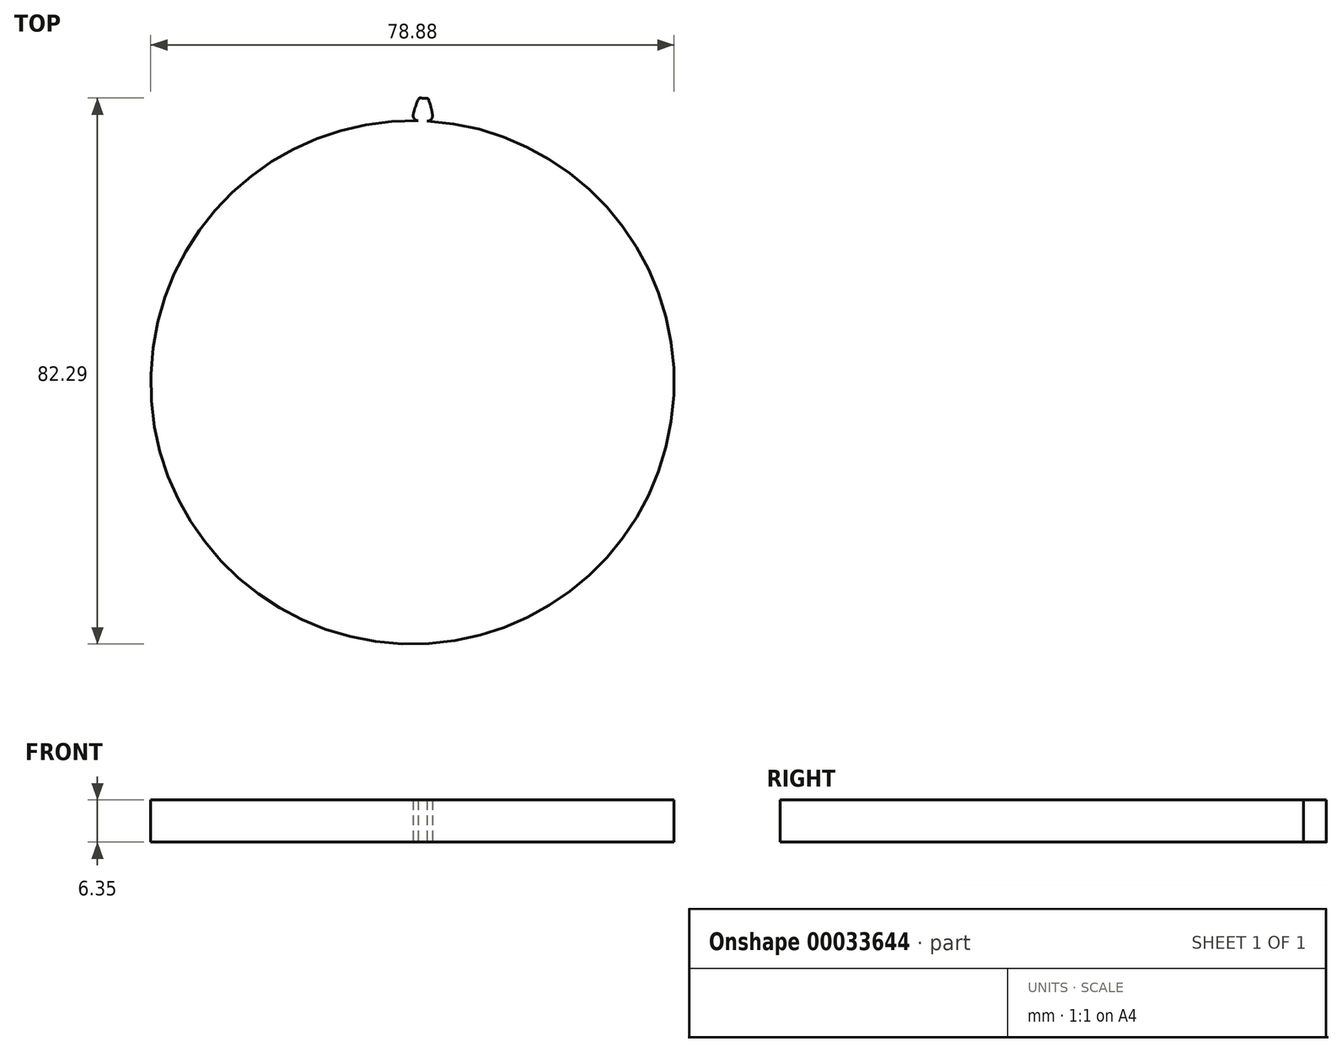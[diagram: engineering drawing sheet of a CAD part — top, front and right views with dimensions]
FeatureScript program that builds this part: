
annotation { "Feature Type Name" : "Feature", "Feature Type Description" : "" }
export const myFeature = defineFeature(function(context is Context, id is Id, definition is map)
    precondition{}
    {
        {
            assignVariable(context, id + "F0", {"name" : "N", "anyValue" : 16 * 3.25});
        }
        {
            var Q0;
            Q0=qCreatedBy(makeId("Top.planeOp"),FACE);
            var sketch = newSketch(context, id + "F1", { "sketchPlane" : qUnion([Q0])});
            skCircle(sketch, "E0", {"center": v(0, 0) * mm, "radius": 39.47 * mm, "construction": true});
            skCircle(sketch, "E1", {"center": v(0, 0) * mm, "radius": 41.28 * mm, "construction": true});
            skCircle(sketch, "E2", {"center": v(0, 0) * mm, "radius": 42.86 * mm});
            skLineSegment(sketch, "E3", {"start": v(0, 0) * mm, "end": v(0, 39.47) * mm, "construction": true});
            skLineSegment(sketch, "E4", {"start": v(0, 0) * mm, "end": v(2.58, 39.39) * mm, "construction": true});
            skLineSegment(sketch, "E5", {"start": v(0, 0) * mm, "end": v(5.15, 39.13) * mm, "construction": true});
            skLineSegment(sketch, "E6", {"start": v(0, 0) * mm, "end": v(7.7, 38.71) * mm, "construction": true});
            skLineSegment(sketch, "E7", {"start": v(0, 0) * mm, "end": v(10.22, 38.13) * mm, "construction": true});
            skCircle(sketch, "E8", {"center": v(0, 0) * mm, "radius": 39.44 * mm});
            skLineSegment(sketch, "E9", {"start": v(2.58, 39.39) * mm, "end": v(0, 39.56) * mm, "construction": true});
            skLineSegment(sketch, "E10", {"start": v(5.15, 39.13) * mm, "end": v(0.03, 39.8) * mm, "construction": true});
            skLineSegment(sketch, "E11", {"start": v(7.7, 38.71) * mm, "end": v(0.1, 40.23) * mm, "construction": true});
            skLineSegment(sketch, "E12", {"start": v(10.22, 38.13) * mm, "end": v(0.23, 40.8) * mm, "construction": true});
            skLineSegment(sketch, "E13", {"start": v(0, 0) * mm, "end": v(12.69, 37.38) * mm, "construction": true});
            skLineSegment(sketch, "E14", {"start": v(12.69, 37.38) * mm, "end": v(0.46, 41.53) * mm, "construction": true});
            skLineSegment(sketch, "E15", {"start": v(0, 0) * mm, "end": v(15.1, 36.47) * mm, "construction": true});
            skLineSegment(sketch, "E16", {"start": v(0, 0) * mm, "end": v(17.46, 35.4) * mm, "construction": true});
            skLineSegment(sketch, "E17", {"start": v(0, 0) * mm, "end": v(19.74, 34.18) * mm, "construction": true});
            skLineSegment(sketch, "E18", {"start": v(15.1, 36.47) * mm, "end": v(0.78, 42.4) * mm, "construction": true});
            skLineSegment(sketch, "E19", {"start": v(17.46, 35.4) * mm, "end": v(1.24, 43.4) * mm, "construction": true});
            skLineSegment(sketch, "E20", {"start": v(19.74, 34.18) * mm, "end": v(1.84, 44.52) * mm, "construction": true});
            skLineSegment(sketch, "E21", {"start": v(0, 0) * mm, "end": v(21.93, 32.82) * mm, "construction": true});
            skLineSegment(sketch, "E22", {"start": v(0, 0) * mm, "end": v(24.03, 31.31) * mm, "construction": true});
            skLineSegment(sketch, "E23", {"start": v(0, 0) * mm, "end": v(26.03, 29.68) * mm, "construction": true});
            skLineSegment(sketch, "E24", {"start": v(0, 0) * mm, "end": v(27.91, 27.91) * mm, "construction": true});
            skLineSegment(sketch, "E25", {"start": v(0, 0) * mm, "end": v(29.68, 26.03) * mm, "construction": true});
            skLineSegment(sketch, "E26", {"start": v(21.93, 32.82) * mm, "end": v(2.6, 45.74) * mm, "construction": true});
            skLineSegment(sketch, "E27", {"start": v(24.03, 31.31) * mm, "end": v(3.53, 47.04) * mm, "construction": true});
            skLineSegment(sketch, "E28", {"start": v(26.03, 29.68) * mm, "end": v(4.66, 48.41) * mm, "construction": true});
            skLineSegment(sketch, "E29", {"start": v(27.91, 27.91) * mm, "end": v(5.99, 49.83) * mm, "construction": true});
            skLineSegment(sketch, "E30", {"start": v(29.68, 26.03) * mm, "end": v(7.53, 51.28) * mm, "construction": true});
            skLineSegment(sketch, "E31", {"start": v(0, 0) * mm, "end": v(31.31, 24.03) * mm, "construction": true});
            skLineSegment(sketch, "E32", {"start": v(31.31, 24.03) * mm, "end": v(9.3, 52.72) * mm, "construction": true});
            skLineSegment(sketch, "E33", {"start": v(0, 0) * mm, "end": v(32.82, 21.93) * mm, "construction": true});
            skLineSegment(sketch, "E34", {"start": v(32.82, 21.93) * mm, "end": v(11.3, 54.15) * mm, "construction": true});
            skSolve(sketch);
        }
        {
            var Q0;
            Q0=qCreatedBy(makeId("Top.planeOp"),FACE);
            var sketch = newSketch(context, id + "F2", { "sketchPlane" : qUnion([Q0])});
            skLineSegment(sketch, "E35.0", {"start": v(31.31, 24.03) * mm, "end": v(9.3, 52.72) * mm, "construction": true});
            skLineSegment(sketch, "E35.1", {"start": v(29.68, 26.03) * mm, "end": v(7.53, 51.28) * mm, "construction": true});
            skLineSegment(sketch, "E35.2", {"start": v(27.91, 27.91) * mm, "end": v(5.99, 49.83) * mm, "construction": true});
            skLineSegment(sketch, "E35.3", {"start": v(26.03, 29.68) * mm, "end": v(4.66, 48.41) * mm, "construction": true});
            skLineSegment(sketch, "E35.4", {"start": v(24.03, 31.31) * mm, "end": v(3.53, 47.04) * mm, "construction": true});
            skLineSegment(sketch, "E35.5", {"start": v(21.93, 32.82) * mm, "end": v(2.6, 45.74) * mm, "construction": true});
            skLineSegment(sketch, "E35.6", {"start": v(19.74, 34.18) * mm, "end": v(1.84, 44.52) * mm, "construction": true});
            skLineSegment(sketch, "E35.7", {"start": v(17.46, 35.4) * mm, "end": v(1.24, 43.4) * mm, "construction": true});
            skLineSegment(sketch, "E35.8", {"start": v(15.1, 36.47) * mm, "end": v(0.78, 42.4) * mm, "construction": true});
            skLineSegment(sketch, "E35.9", {"start": v(12.69, 37.38) * mm, "end": v(0.46, 41.53) * mm, "construction": true});
            skLineSegment(sketch, "E35.10", {"start": v(10.22, 38.13) * mm, "end": v(0.23, 40.8) * mm, "construction": true});
            skLineSegment(sketch, "E35.11", {"start": v(7.7, 38.71) * mm, "end": v(0.1, 40.23) * mm, "construction": true});
            skLineSegment(sketch, "E35.12", {"start": v(5.15, 39.13) * mm, "end": v(0.03, 39.8) * mm, "construction": true});
            skLineSegment(sketch, "E35.13", {"start": v(2.58, 39.39) * mm, "end": v(0, 39.56) * mm, "construction": true});
            skCircle(sketch, "E35.14", {"center": v(0, 0) * mm, "radius": 39.47 * mm});
            skCircle(sketch, "E35.15", {"center": v(0, 0) * mm, "radius": 39.44 * mm});
            skCircle(sketch, "E35.16", {"center": v(0, 0) * mm, "radius": 41.28 * mm, "construction": true});
            skCircle(sketch, "E35.17", {"center": v(0, 0) * mm, "radius": 42.86 * mm});
            skLineSegment(sketch, "E36.0", {"start": v(32.82, 21.93) * mm, "end": v(11.3, 54.15) * mm, "construction": true});
            skLineSegment(sketch, "E37.0", {"start": v(0, 0) * mm, "end": v(0, 39.47) * mm, "construction": true});
            skFitSpline(sketch, "E38", {"points": [v(0, 39.47) * mm, v(0, 39.56) * mm, v(0.03, 39.8) * mm, v(0.1, 40.23) * mm, v(0.23, 40.8) * mm, v(0.46, 41.53) * mm, v(0.78, 42.4) * mm, v(1.24, 43.4) * mm, v(1.84, 44.52) * mm, v(2.6, 45.74) * mm, v(3.53, 47.04) * mm, v(4.66, 48.41) * mm, v(5.99, 49.83) * mm, v(7.53, 51.28) * mm, v(9.3, 52.72) * mm, v(11.3, 54.15) * mm, v(0, 0) * mm], "startDerivative": vector(0.89, 20.38) * mm, "endDerivative": vector(-106.5, -510.77) * mm});
            skLineSegment(sketch, "E39", {"start": v(0.37, 41.27) * mm, "end": v(0, 0) * mm, "construction": true});
            skLineSegment(sketch, "E40", {"start": v(0, 0) * mm, "end": v(1.68, 42.83) * mm, "construction": true});
            skFitSpline(sketch, "E41.MirrorCS", {"points": [v(3.1, 39.35) * mm, v(3.1, 39.43) * mm, v(3.1, 39.69) * mm, v(3.05, 40.1) * mm, v(2.96, 40.7) * mm, v(2.8, 41.44) * mm, v(2.54, 42.33) * mm, v(2.17, 43.36) * mm, v(1.66, 44.52) * mm, v(1, 45.8) * mm, v(0.16, 47.17) * mm, v(-0.85, 48.63) * mm, v(-2.07, 50.15) * mm, v(-3.5, 51.7) * mm, v(-5.14, 53.29) * mm, v(-7.01, 54.87) * mm, v(0, 0) * mm], "startDerivative": vector(0.71, 20.38) * mm, "endDerivative": vector(66.14, -517.54) * mm});
            skLineSegment(sketch, "E42", {"start": v(3.1, 39.35) * mm, "end": v(3.1, 39.32) * mm});
            skLineSegment(sketch, "E43", {"start": v(0, 39.47) * mm, "end": v(0, 39.44) * mm});
            skSolve(sketch);
        }
        {
            var Q0;
            {var subQ3=sQuery(id+"F2.wireOp",EDGE,"E41.MirrorCS");var subQ6=sQuery(id+"F2.wireOp",EDGE,"E35.17");var subQ8=makeQuery(id+"F2.imprint","INTERSECT",VERTEX,{"disambiguationData":[OD(1.0)],"derivedFrom":[subQ6,subQ3]});Q0=makeQuery(id+"F2.imprint","IMPRINT",FACE,{"disambiguationData":[TD([[makeQuery(id+"F2.imprint","IMPRINT",EDGE,{"disambiguationData":[TD([[subQ8,-1.0]])],"derivedFrom":subQ6}),1.0]])]});}
            var Q1;
            {var subQ3=sQuery(id+"F2.wireOp",EDGE,"E41.MirrorCS");var subQ5=sQuery(id+"F2.wireOp",EDGE,"E35.15");var subQ6=makeQuery(id+"F2.imprint","INTERSECT",VERTEX,{"derivedFrom":[subQ5,subQ3]});Q1=makeQuery(id+"F2.imprint","IMPRINT",FACE,{"disambiguationData":[TD([[makeQuery(id+"F2.imprint","IMPRINT",EDGE,{"disambiguationData":[TD([[subQ6,-1.0]])],"derivedFrom":subQ5}),1.0]])]});}
            var Q2;
            {var subQ2=sQuery(id+"F2.wireOp",EDGE,"E42");Q2=makeQuery(id+"F2.imprint","IMPRINT",FACE,{"disambiguationData":[TD([[makeQuery(id+"F2.imprint","IMPRINT",EDGE,{"derivedFrom":subQ2}),-1.0]])]});}
            extrude(context, id + "F3", {"entities" : qUnion([Q0, Q1, Q2]), "depth" : 6.35 * mm, "offsetDistance" : 25.4 * mm});
        }
        {
            var Q0;
            Q0=makeQuery(id+"F3.opExtrude","SWEPT_EDGE",EDGE,{"disambiguationData":[OSD([sQuery(id+"F2.wireOp",EDGE,"E35.17"),sQuery(id+"F2.wireOp",EDGE,"E38")])]});
            var Q1;
            Q1=makeQuery(id+"F3.opExtrude","SWEPT_EDGE",EDGE,{"disambiguationData":[OSD([sQuery(id+"F2.wireOp",EDGE,"E35.17"),sQuery(id+"F2.wireOp",EDGE,"E41.MirrorCS")])]});
            fillet(context, id + "F4", {"entities" : qUnion([Q0, Q1]), "radius" : 0.25 * mm, "tangentPropagation" : true, "allowEdgeOverflow" : false});
        }
        {
            var Q0;
            Q0=makeQuery(id+"F3.opExtrude","SWEPT_EDGE",EDGE,{"disambiguationData":[OSD([sQuery(id+"F2.wireOp",EDGE,"E35.15"),sQuery(id+"F2.wireOp",EDGE,"E42")])]});
            var Q1;
            Q1=makeQuery(id+"F3.opExtrude","SWEPT_EDGE",EDGE,{"disambiguationData":[OSD([sQuery(id+"F2.wireOp",EDGE,"E35.15"),sQuery(id+"F2.wireOp",EDGE,"E43")])]});
            fillet(context, id + "F5", {"entities" : qUnion([Q0, Q1]), "radius" : 0.8 * mm, "tangentPropagation" : true, "allowEdgeOverflow" : false});
        }
        {
            var Q0;
            Q0=qCreatedBy(makeId("Right.planeOp"),FACE);
            var sketch = newSketch(context, id + "F6", { "sketchPlane" : qUnion([Q0])});
            skLineSegment(sketch, "E44", {"start": v(0, 0) * mm, "end": v(0, 43.3) * mm, "construction": true});
            skSolve(sketch);
        }
        {
            var Q0;
            Q0=makeQuery(id+"F3.opExtrude","SWEPT_BODY",BODY,{"disambiguationData":[OSD([sQuery(id+"F2.wireOp",EDGE,"E35.15"),sQuery(id+"F2.wireOp",EDGE,"E35.17"),sQuery(id+"F2.wireOp",EDGE,"E38"),sQuery(id+"F2.wireOp",EDGE,"E41.MirrorCS"),sQuery(id+"F2.wireOp",EDGE,"9305e2c8-a00a-4cbc-a3b2-8fc88bc1717c"),sQuery(id+"F2.wireOp",EDGE,"f762f43d-eaf9-45ff-b6cd-062fd530227c")])]});
            var Q1;
            Q1=sQuery(id+"F6.wireOp",EDGE,"E44");
            circularPattern(context, id + "F7", {"operationType" : NewBodyOperationType.ADD, "entities" : qUnion([Q0]), "axis" : qUnion([Q1]), "angle" : (360 / getVariable(context, 'N')) * degree, "instanceCount" : getVariable(context, 'N'), "oppositeDirection" : true});
        }
    });
